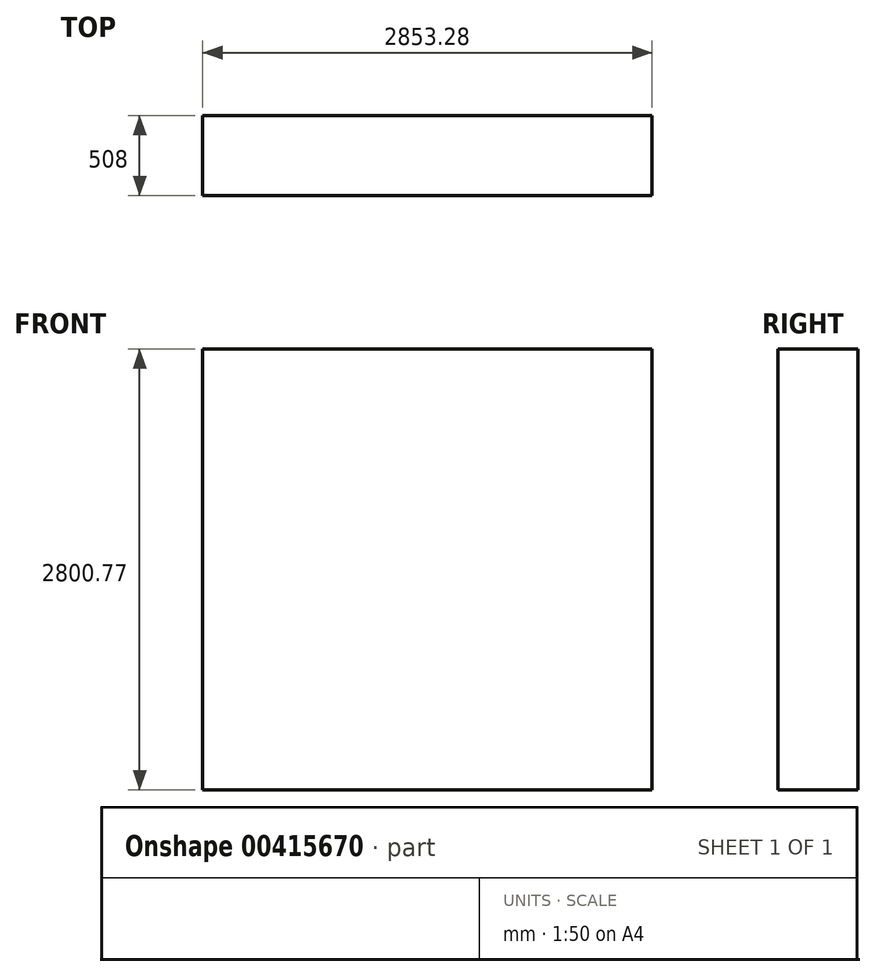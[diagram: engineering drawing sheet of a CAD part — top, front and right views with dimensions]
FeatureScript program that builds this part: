
annotation { "Feature Type Name" : "Feature", "Feature Type Description" : "" }
export const myFeature = defineFeature(function(context is Context, id is Id, definition is map)
    precondition{}
    {
        {
            var Q0;
            Q0=qCreatedBy(makeId("Front.planeOp"),FACE);
            var sketch = newSketch(context, id + "F0", { "sketchPlane" : qUnion([Q0])});
            skLineSegment(sketch, "E0.bottom", {"start": v(-52.72, -42.62) * mm, "end": v(57.36, -42.62) * mm});
            skLineSegment(sketch, "E0.top", {"start": v(-52.72, 14.95) * mm, "end": v(57.36, 14.95) * mm});
            skLineSegment(sketch, "E0.left", {"start": v(-52.72, -42.62) * mm, "end": v(-52.72, 14.95) * mm});
            skLineSegment(sketch, "E0.right", {"start": v(57.36, -42.62) * mm, "end": v(57.36, 14.95) * mm});
            skLineSegment(sketch, "E1.bottom", {"start": v(57.36, -42.62) * mm, "end": v(-47.37, -42.62) * mm});
            skLineSegment(sketch, "E1.top", {"start": v(57.36, -42.62) * mm, "end": v(-47.37, -42.62) * mm});
            skLineSegment(sketch, "E1.left", {"start": v(57.36, -42.62) * mm, "end": v(57.36, -42.62) * mm});
            skLineSegment(sketch, "E1.right", {"start": v(-47.37, -42.62) * mm, "end": v(-47.37, -42.62) * mm});
            skLineSegment(sketch, "E2.left", {"start": v(-52.72, -42.62) * mm, "end": v(-52.72, -42.62) * mm});
            skLineSegment(sketch, "E3.bottom", {"start": v(57.36, -42.62) * mm, "end": v(-52.72, -42.62) * mm});
            skLineSegment(sketch, "E3.top", {"start": v(57.36, -42.62) * mm, "end": v(-52.72, -42.62) * mm});
            skSolve(sketch);
        }
        {
            var Q0;
            Q0=makeQuery(id+"F0.imprint","IMPRINT",FACE,{"disambiguationData":[TD([[makeQuery(id+"F0.imprint","IMPRINT",EDGE,{"derivedFrom":sQuery(id+"F0.wireOp",EDGE,"E0.top")}),-1.0]])]});
            extrude(context, id + "F1", {"entities" : qUnion([Q0]), "depth" : 508 * mm});
        }
        {
            var Q0;
            Q0=makeQuery(id+"F1.opExtrude","SWEPT_FACE",FACE,{"disambiguationData":[OSD([sQuery(id+"F0.wireOp",EDGE,"E0.top")])]});
            extrude(context, id + "F2", {"entities" : qUnion([Q0]), "operationType" : NewBodyOperationType.ADD, "depth" : 2743.2 * mm, "hasSecondDirection" : true, "secondDirectionOppositeDirection" : true, "secondDirectionDepth" : 25.4 * mm});
        }
        {
            var Q0;
            {var subQ0=sQuery(id+"F0.wireOp",EDGE,"E0.left");Q0=makeQuery(id+"F2.boolean.opBoolean","MERGE",FACE,{"derivedFrom":[makeQuery(id+"F1.opExtrude","SWEPT_FACE",FACE,{"disambiguationData":[OSD([subQ0])]}),makeQuery(id+"F2.opExtrude","SWEPT_FACE",FACE,{"disambiguationData":[OSD([sQuery(id+"F0.wireOp",EDGE,"E0.top"),subQ0])]})]});}
            extrude(context, id + "F3", {"entities" : qUnion([Q0]), "operationType" : NewBodyOperationType.ADD, "depth" : 2743.2 * mm});
        }
    });
